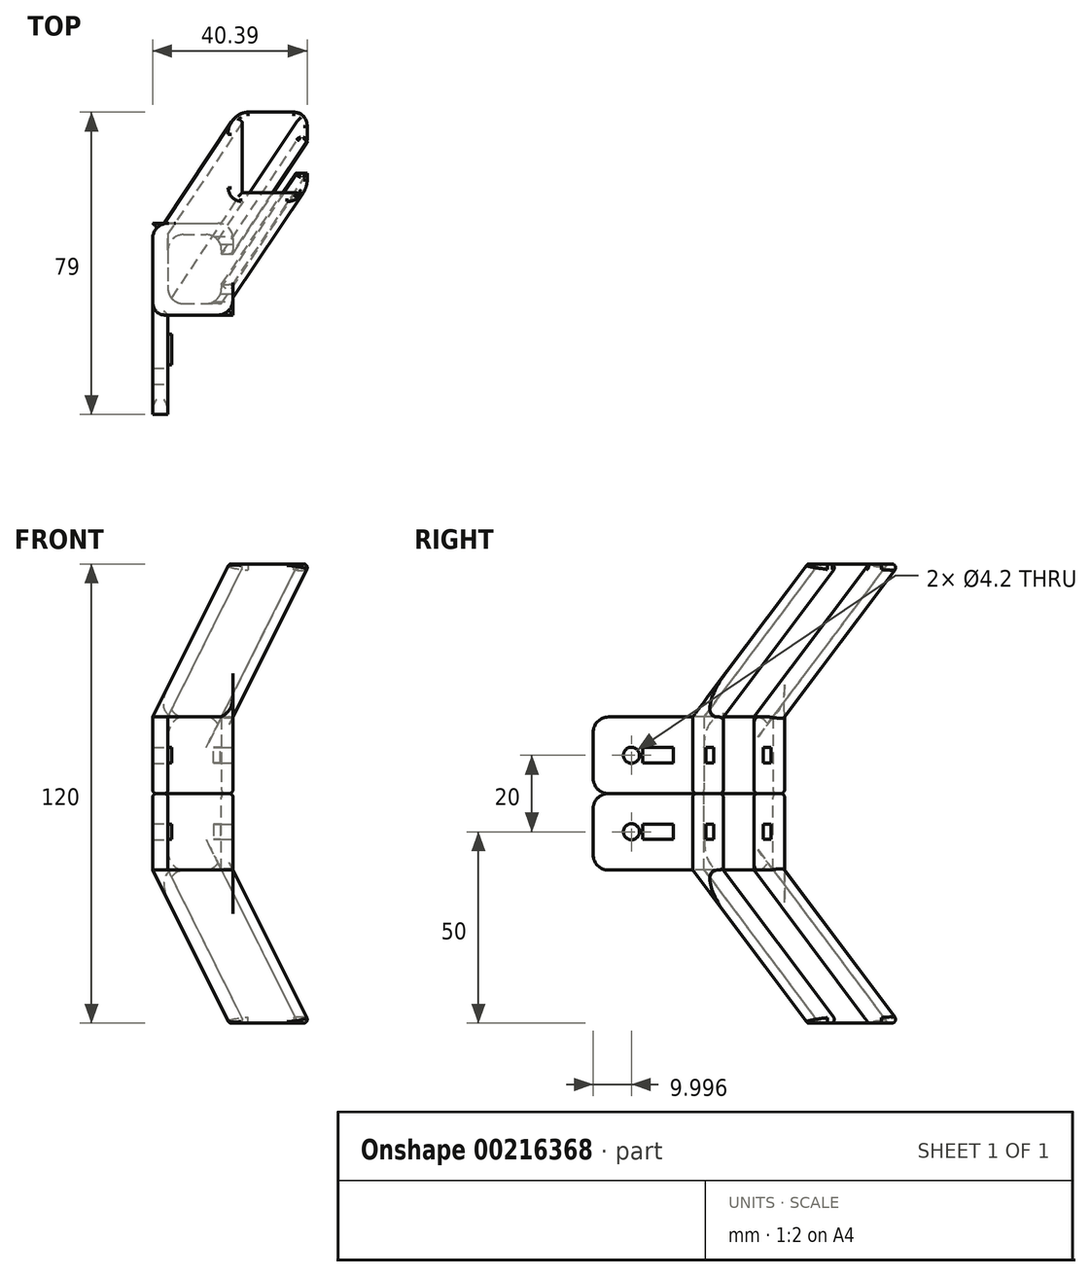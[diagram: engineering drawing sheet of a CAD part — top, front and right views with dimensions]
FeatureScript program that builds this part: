
annotation { "Feature Type Name" : "Feature", "Feature Type Description" : "" }
export const myFeature = defineFeature(function(context is Context, id is Id, definition is map)
    precondition{}
    {
        {
            var Q0;
            Q0=qCreatedBy(makeId("Top.planeOp"),FACE);
            var sketch = newSketch(context, id + "F0", { "sketchPlane" : qUnion([Q0])});
            skLineSegment(sketch, "E0.bottom", {"start": v(-48.62, 57.86) * mm, "end": v(-44.62, 57.86) * mm});
            skLineSegment(sketch, "E0.top", {"start": v(-48.62, 7.86) * mm, "end": v(-44.62, 7.86) * mm});
            skLineSegment(sketch, "E0.left", {"start": v(-48.62, 57.86) * mm, "end": v(-48.62, 7.86) * mm});
            skLineSegment(sketch, "E0.right", {"start": v(-44.62, 33.86) * mm, "end": v(-44.62, 7.86) * mm});
            skLineSegment(sketch, "E1.bottom", {"start": v(-44.62, 57.86) * mm, "end": v(-27.62, 57.86) * mm});
            skLineSegment(sketch, "E1.top", {"start": v(-44.62, 33.86) * mm, "end": v(-27.62, 33.86) * mm});
            skLineSegment(sketch, "E1.right", {"start": v(-27.62, 57.86) * mm, "end": v(-27.62, 49.86) * mm});
            skLineSegment(sketch, "E2.bottom", {"start": v(-44.62, 54.86) * mm, "end": v(-30.62, 54.86) * mm});
            skLineSegment(sketch, "E2.top", {"start": v(-44.62, 36.86) * mm, "end": v(-30.62, 36.86) * mm});
            skLineSegment(sketch, "E2.left", {"start": v(-44.62, 54.86) * mm, "end": v(-44.62, 36.86) * mm});
            skLineSegment(sketch, "E2.right", {"start": v(-30.62, 54.86) * mm, "end": v(-30.62, 49.86) * mm});
            skLineSegment(sketch, "E3", {"start": v(-30.62, 49.86) * mm, "end": v(-27.62, 49.86) * mm});
            skLineSegment(sketch, "E4", {"start": v(-30.62, 41.86) * mm, "end": v(-27.62, 41.86) * mm});
            skLineSegment(sketch, "E5.trimOffspring", {"start": v(-27.62, 41.86) * mm, "end": v(-27.62, 33.86) * mm});
            skLineSegment(sketch, "E6.trimOffspring", {"start": v(-30.62, 41.86) * mm, "end": v(-30.62, 36.86) * mm});
            skSolve(sketch);
        }
        {
            var Q0;
            Q0 = qSketchRegion(id + "F0", true);
            extrude(context, id + "F1", {"entities" : qUnion([Q0]), "depth" : 20 * mm, "offsetDistance" : 25 * mm});
        }
        {
            var Q0;
            Q0=makeQuery(id+"F1.opExtrude","SWEPT_FACE",FACE,{"disambiguationData":[OSD([sQuery(id+"F0.wireOp",EDGE,"E0.right")])]});
            var sketch = newSketch(context, id + "F2", { "sketchPlane" : qUnion([Q0])});
            skCircle(sketch, "E7", {"center": v(17.86, 10) * mm, "radius": 2.1 * mm});
            skPoint(sketch, "E7.centerSnap0", {"position": v(7.86, 10) * mm});
            skLineSegment(sketch, "E8.bottom", {"start": v(28.86, 12) * mm, "end": v(20.86, 12) * mm});
            skLineSegment(sketch, "E8.top", {"start": v(28.86, 8) * mm, "end": v(20.86, 8) * mm});
            skLineSegment(sketch, "E8.left", {"start": v(28.86, 12) * mm, "end": v(28.86, 8) * mm});
            skLineSegment(sketch, "E8.right", {"start": v(20.86, 12) * mm, "end": v(20.86, 8) * mm});
            skSolve(sketch);
        }
        {
            var Q0;
            Q0=makeQuery(id+"F2.imprint","IMPRINT",FACE,{"disambiguationData":[TD([[makeQuery(id+"F2.imprint","IMPRINT",EDGE,{"derivedFrom":sQuery(id+"F2.wireOp",EDGE,"E7")}),1.0]])]});
            extrude(context, id + "F3", {"entities" : qUnion([Q0]), "operationType" : NewBodyOperationType.REMOVE, "oppositeDirection" : true, "depth" : 25 * mm, "offsetDistance" : 25 * mm});
        }
        {
            var Q0;
            Q0=makeQuery(id+"F1.opExtrude","SWEPT_FACE",FACE,{"disambiguationData":[OSD([sQuery(id+"F0.wireOp",EDGE,"E1.right")])]});
            var sketch = newSketch(context, id + "F4", { "sketchPlane" : qUnion([Q0])});
            skLineSegment(sketch, "E9.bottom", {"start": v(54.36, 12) * mm, "end": v(52.36, 12) * mm});
            skLineSegment(sketch, "E9.top", {"start": v(54.36, 8) * mm, "end": v(52.36, 8) * mm});
            skLineSegment(sketch, "E9.left", {"start": v(54.36, 12) * mm, "end": v(54.36, 8) * mm});
            skLineSegment(sketch, "E9.right", {"start": v(52.36, 12) * mm, "end": v(52.36, 8) * mm});
            skSolve(sketch);
        }
        {
            var Q0;
            Q0=makeQuery(id+"F1.opExtrude","SWEPT_FACE",FACE,{"disambiguationData":[OSD([sQuery(id+"F0.wireOp",EDGE,"E5.trimOffspring")])]});
            var sketch = newSketch(context, id + "F5", { "sketchPlane" : qUnion([Q0])});
            skLineSegment(sketch, "E10.bottom", {"start": v(39.36, 12) * mm, "end": v(37.36, 12) * mm});
            skLineSegment(sketch, "E10.top", {"start": v(39.36, 8) * mm, "end": v(37.36, 8) * mm});
            skLineSegment(sketch, "E10.left", {"start": v(39.36, 12) * mm, "end": v(39.36, 8) * mm});
            skLineSegment(sketch, "E10.right", {"start": v(37.36, 12) * mm, "end": v(37.36, 8) * mm});
            skSolve(sketch);
        }
        {
            var Q0;
            Q0=makeQuery(id+"F4.imprint","IMPRINT",FACE,{"disambiguationData":[TD([[makeQuery(id+"F4.imprint","IMPRINT",EDGE,{"derivedFrom":sQuery(id+"F4.wireOp",EDGE,"E9.bottom")}),1.0]])]});
            var Q1;
            Q1=makeQuery(id+"F5.imprint","IMPRINT",FACE,{"disambiguationData":[TD([[makeQuery(id+"F5.imprint","IMPRINT",EDGE,{"derivedFrom":sQuery(id+"F5.wireOp",EDGE,"E10.bottom")}),1.0]])]});
            extrude(context, id + "F6", {"entities" : qUnion([Q0, Q1]), "operationType" : NewBodyOperationType.REMOVE, "oppositeDirection" : true, "depth" : 4 * mm, "offsetDistance" : 25 * mm});
        }
        {
            var Q0;
            Q0=makeQuery(id+"F1.opExtrude","CAP_FACE",FACE,{"disambiguationData":[OSD([sQuery(id+"F0.wireOp",EDGE,"E0.bottom"),sQuery(id+"F0.wireOp",EDGE,"E0.top"),sQuery(id+"F0.wireOp",EDGE,"E0.left"),sQuery(id+"F0.wireOp",EDGE,"E0.right"),sQuery(id+"F0.wireOp",EDGE,"E1.bottom"),sQuery(id+"F0.wireOp",EDGE,"E1.top"),sQuery(id+"F0.wireOp",EDGE,"E1.right"),sQuery(id+"F0.wireOp",EDGE,"E2.bottom"),sQuery(id+"F0.wireOp",EDGE,"E2.top"),sQuery(id+"F0.wireOp",EDGE,"E2.left"),sQuery(id+"F0.wireOp",EDGE,"E2.right"),sQuery(id+"F0.wireOp",EDGE,"E3"),sQuery(id+"F0.wireOp",EDGE,"E4"),sQuery(id+"F0.wireOp",EDGE,"E5.trimOffspring"),sQuery(id+"F0.wireOp",EDGE,"E6.trimOffspring")])],"isStart":false});
            var sketch = newSketch(context, id + "F7", { "sketchPlane" : qUnion([Q0])});
            skLineSegment(sketch, "E11", {"start": v(-44.62, 33.86) * mm, "end": v(-48.62, 33.86) * mm});
            skSolve(sketch);
        }
        {
            var Q0;
            Q0=makeQuery(id+"F1.opExtrude","CAP_FACE",FACE,{"disambiguationData":[OSD([sQuery(id+"F0.wireOp",EDGE,"E0.bottom"),sQuery(id+"F0.wireOp",EDGE,"E0.top"),sQuery(id+"F0.wireOp",EDGE,"E0.left"),sQuery(id+"F0.wireOp",EDGE,"E0.right"),sQuery(id+"F0.wireOp",EDGE,"E1.bottom"),sQuery(id+"F0.wireOp",EDGE,"E1.top"),sQuery(id+"F0.wireOp",EDGE,"E1.right"),sQuery(id+"F0.wireOp",EDGE,"E2.bottom"),sQuery(id+"F0.wireOp",EDGE,"E2.top"),sQuery(id+"F0.wireOp",EDGE,"E2.left"),sQuery(id+"F0.wireOp",EDGE,"E2.right"),sQuery(id+"F0.wireOp",EDGE,"E3"),sQuery(id+"F0.wireOp",EDGE,"E4"),sQuery(id+"F0.wireOp",EDGE,"E5.trimOffspring"),sQuery(id+"F0.wireOp",EDGE,"E6.trimOffspring")])],"isStart":false});
            cPlane(context, id + "F8", {"entities" : qUnion([Q0]), "cplaneType" : CPlaneType.OFFSET, "offset" : 40 * mm, "width" : 150 * mm, "height" : 150 * mm});
        }
        {
            var Q0;
            Q0=qCreatedBy(id+"F8.planeOp",FACE);
            var sketch = newSketch(context, id + "F9", { "sketchPlane" : qUnion([Q0])});
            skLineSegment(sketch, "E12.bottom", {"start": v(-28.62, 87.86) * mm, "end": v(-7.62, 87.86) * mm});
            skLineSegment(sketch, "E12.top", {"start": v(-28.62, 63.86) * mm, "end": v(-7.62, 63.86) * mm});
            skLineSegment(sketch, "E12.left", {"start": v(-28.62, 87.86) * mm, "end": v(-28.62, 63.86) * mm});
            skLineSegment(sketch, "E12.right", {"start": v(-7.62, 87.86) * mm, "end": v(-7.62, 79.86) * mm});
            skLineSegment(sketch, "E13.bottom", {"start": v(-24.62, 84.86) * mm, "end": v(-10.62, 84.86) * mm});
            skLineSegment(sketch, "E13.top", {"start": v(-24.62, 66.86) * mm, "end": v(-10.62, 66.86) * mm});
            skLineSegment(sketch, "E13.left", {"start": v(-24.62, 84.86) * mm, "end": v(-24.62, 66.86) * mm});
            skLineSegment(sketch, "E13.right", {"start": v(-10.62, 84.86) * mm, "end": v(-10.62, 79.86) * mm});
            skLineSegment(sketch, "E14", {"start": v(-7.62, 71.86) * mm, "end": v(-10.62, 71.86) * mm});
            skLineSegment(sketch, "E15", {"start": v(-7.62, 79.86) * mm, "end": v(-10.62, 79.86) * mm});
            skLineSegment(sketch, "E16.trimOffspring", {"start": v(-10.62, 71.86) * mm, "end": v(-10.62, 66.86) * mm});
            skLineSegment(sketch, "E17.trimOffspring", {"start": v(-7.62, 71.86) * mm, "end": v(-7.62, 63.86) * mm});
            skPoint(sketch, "E18", {"position": v(-24.62, 63.86) * mm});
            skSolve(sketch);
        }
        {
            var Q1;
            {var subQ0=sQuery(id+"F7.wireOp",EDGE,"E11");Q1=makeQuery(id+"F7.imprint","IMPRINT",FACE,{"disambiguationData":[TD([[makeQuery(id+"F7.imprint","IMPRINT",EDGE,{"derivedFrom":subQ0}),-1.0]])]});}
            var Q2;
            Q2=makeQuery(id+"F9.imprint","IMPRINT",FACE,{"disambiguationData":[TD([[makeQuery(id+"F9.imprint","IMPRINT",EDGE,{"derivedFrom":sQuery(id+"F9.wireOp",EDGE,"E12.bottom")}),-1.0]])]});
            var Q3;
            Q3=sQuery(id+"F7.wireOp",VERTEX,"E11.start");
            var Q4;
            Q4=sQuery(id+"F9.wireOp",VERTEX,"E18");
            loft(context, id + "F10", {"operationType" : NewBodyOperationType.ADD, "sheetProfilesArray" : [{ "sheetProfileEntities" : qUnion([Q1]) }, { "sheetProfileEntities" : qUnion([Q2]) }], "matchConnections" : true, "connections" : [{ "connectionEntities" : qUnion([Q3, Q4]), "connectionEdgeQueries" : qUnion([]), "connectionEdgeParameters" : [] }]});
        }
        {
            var Q0;
            Q0=makeQuery(id+"F1.opExtrude","CAP_EDGE",EDGE,{"disambiguationData":[OSD([sQuery(id+"F0.wireOp",EDGE,"E0.top")])],"isStart":false});
            var Q1;
            Q1=makeQuery(id+"F1.opExtrude","CAP_EDGE",EDGE,{"disambiguationData":[OSD([sQuery(id+"F0.wireOp",EDGE,"E0.top")])],"isStart":true});
            var Q2;
            Q2=makeQuery(id+"F1.opExtrude","SWEPT_EDGE",EDGE,{"disambiguationData":[OSD([sQuery(id+"F0.wireOp",EDGE,"E2.top"),sQuery(id+"F0.wireOp",EDGE,"E6.trimOffspring")])]});
            var Q3;
            Q3=makeQuery(id+"F1.opExtrude","SWEPT_EDGE",EDGE,{"disambiguationData":[OSD([sQuery(id+"F0.wireOp",EDGE,"E2.bottom"),sQuery(id+"F0.wireOp",EDGE,"E2.right")])]});
            var Q4;
            Q4=makeQuery(id+"F1.opExtrude","SWEPT_EDGE",EDGE,{"disambiguationData":[OSD([sQuery(id+"F0.wireOp",EDGE,"E2.bottom"),sQuery(id+"F0.wireOp",EDGE,"E2.left")])]});
            var Q5;
            Q5=makeQuery(id+"F1.opExtrude","SWEPT_EDGE",EDGE,{"disambiguationData":[OSD([sQuery(id+"F0.wireOp",EDGE,"E2.top"),sQuery(id+"F0.wireOp",EDGE,"E2.left")])]});
            var Q6;
            Q6=makeQuery(id+"F10.opLoft","SWEPT_EDGE",EDGE,{"disambiguationData":[OSD([sQuery(id+"F0.wireOp",EDGE,"E0.bottom"),sQuery(id+"F0.wireOp",EDGE,"E1.bottom"),sQuery(id+"F0.wireOp",EDGE,"E1.right"),sQuery(id+"F9.wireOp",EDGE,"E12.bottom"),sQuery(id+"F9.wireOp",EDGE,"E12.right")])]});
            var Q7;
            Q7=makeQuery(id+"F10.opLoft","SWEPT_EDGE",EDGE,{"disambiguationData":[OSD([sQuery(id+"F0.wireOp",EDGE,"E0.left"),sQuery(id+"F7.wireOp",EDGE,"E11"),sQuery(id+"F9.wireOp",EDGE,"E12.top"),sQuery(id+"F9.wireOp",EDGE,"E12.left")])]});
            var Q8;
            Q8=makeQuery(id+"F1.opExtrude","SWEPT_EDGE",EDGE,{"disambiguationData":[OSD([sQuery(id+"F0.wireOp",EDGE,"E1.bottom"),sQuery(id+"F0.wireOp",EDGE,"E1.right")])]});
            var Q9;
            Q9=makeQuery(id+"F10.opLoft","SWEPT_EDGE",EDGE,{"disambiguationData":[OSD([sQuery(id+"F0.wireOp",EDGE,"E1.top"),sQuery(id+"F0.wireOp",EDGE,"E5.trimOffspring"),sQuery(id+"F9.wireOp",EDGE,"E12.top"),sQuery(id+"F9.wireOp",EDGE,"E17.trimOffspring")])]});
            var Q10;
            Q10=makeQuery(id+"F10.opLoft","SWEPT_EDGE",EDGE,{"disambiguationData":[OSD([sQuery(id+"F0.wireOp",EDGE,"E0.bottom"),sQuery(id+"F0.wireOp",EDGE,"E0.left"),sQuery(id+"F0.wireOp",EDGE,"E1.bottom"),sQuery(id+"F9.wireOp",EDGE,"E12.bottom"),sQuery(id+"F9.wireOp",EDGE,"E12.left")])]});
            fillet(context, id + "F11", {"entities" : qUnion([Q0, Q1, Q2, Q3, Q4, Q5, Q6, Q7, Q8, Q9, Q10]), "radius" : 4 * mm, "allowEdgeOverflow" : false});
        }
        {
            var Q0;
            Q0=makeQuery(id+"F10.opLoft","CAP_FACE",FACE,{"disambiguationData":[OSD([makeQuery(id+"F9.imprint","IMPRINT",FACE,{"disambiguationData":[TD([[makeQuery(id+"F9.imprint","IMPRINT",EDGE,{"derivedFrom":sQuery(id+"F9.wireOp",EDGE,"E12.bottom")}),-1.0]])]})])],"isStart":true});
            var Q1;
            Q1=makeQuery(id+"F1.opExtrude","CAP_FACE",FACE,{"disambiguationData":[OSD([sQuery(id+"F0.wireOp",EDGE,"E0.bottom"),sQuery(id+"F0.wireOp",EDGE,"E0.top"),sQuery(id+"F0.wireOp",EDGE,"E0.left"),sQuery(id+"F0.wireOp",EDGE,"E0.right"),sQuery(id+"F0.wireOp",EDGE,"E1.bottom"),sQuery(id+"F0.wireOp",EDGE,"E1.top"),sQuery(id+"F0.wireOp",EDGE,"E1.right"),sQuery(id+"F0.wireOp",EDGE,"E2.bottom"),sQuery(id+"F0.wireOp",EDGE,"E2.top"),sQuery(id+"F0.wireOp",EDGE,"E2.left"),sQuery(id+"F0.wireOp",EDGE,"E2.right"),sQuery(id+"F0.wireOp",EDGE,"E3"),sQuery(id+"F0.wireOp",EDGE,"E4"),sQuery(id+"F0.wireOp",EDGE,"E5.trimOffspring"),sQuery(id+"F0.wireOp",EDGE,"E6.trimOffspring")])],"isStart":true});
            var Q2;
            Q2=makeQuery(id+"F1.opExtrude","SWEPT_EDGE",EDGE,{"disambiguationData":[OSD([sQuery(id+"F0.wireOp",EDGE,"E4"),sQuery(id+"F0.wireOp",EDGE,"E5.trimOffspring")])]});
            var Q3;
            Q3=makeQuery(id+"F1.opExtrude","SWEPT_EDGE",EDGE,{"disambiguationData":[OSD([sQuery(id+"F0.wireOp",EDGE,"E1.right"),sQuery(id+"F0.wireOp",EDGE,"E3")])]});
            fillet(context, id + "F12", {"entities" : qUnion([Q0, Q1, Q2, Q3]), "radius" : 1 * mm, "allowEdgeOverflow" : false});
        }
        {
            var Q0;
            Q0=makeQuery(id+"F2.imprint","IMPRINT",FACE,{"disambiguationData":[TD([[makeQuery(id+"F2.imprint","IMPRINT",EDGE,{"derivedFrom":sQuery(id+"F2.wireOp",EDGE,"E8.bottom")}),1.0]])]});
            extrude(context, id + "F13", {"entities" : qUnion([Q0]), "operationType" : NewBodyOperationType.ADD, "depth" : 1 * mm, "offsetDistance" : 25 * mm});
        }
        {
            var Q0;
            Q0=makeQuery(id+"F1.opExtrude","SWEPT_BODY",BODY,{"disambiguationData":[OSD([sQuery(id+"F0.wireOp",EDGE,"E0.bottom"),sQuery(id+"F0.wireOp",EDGE,"E0.top"),sQuery(id+"F0.wireOp",EDGE,"E0.left"),sQuery(id+"F0.wireOp",EDGE,"E0.right"),sQuery(id+"F0.wireOp",EDGE,"E1.bottom"),sQuery(id+"F0.wireOp",EDGE,"E1.top"),sQuery(id+"F0.wireOp",EDGE,"E1.right"),sQuery(id+"F0.wireOp",EDGE,"E2.bottom"),sQuery(id+"F0.wireOp",EDGE,"E2.top"),sQuery(id+"F0.wireOp",EDGE,"E2.left"),sQuery(id+"F0.wireOp",EDGE,"E2.right"),sQuery(id+"F0.wireOp",EDGE,"E3"),sQuery(id+"F0.wireOp",EDGE,"E4"),sQuery(id+"F0.wireOp",EDGE,"E5.trimOffspring"),sQuery(id+"F0.wireOp",EDGE,"E6.trimOffspring")])]});
            var Q1;
            Q1=qCreatedBy(makeId("Top.planeOp"),FACE);
            mirror(context, id + "F14", {"entities" : qUnion([Q0]), "mirrorPlane" : qUnion([Q1])});
        }
        {
            var Q0;
            Q0=makeQuery(id+"F1.opExtrude","SWEPT_EDGE",EDGE,{"disambiguationData":[OSD([sQuery(id+"F0.wireOp",EDGE,"E0.bottom"),sQuery(id+"F0.wireOp",EDGE,"E0.left")])]});
            var Q1;
            Q1=makeQuery(id+"F1.opExtrude","SWEPT_EDGE",EDGE,{"disambiguationData":[OSD([sQuery(id+"F0.wireOp",EDGE,"E1.top"),sQuery(id+"F0.wireOp",EDGE,"E5.trimOffspring")])]});
            fillet(context, id + "F15", {"entities" : qUnion([Q0, Q1]), "radius" : 4 * mm, "tangentPropagation" : true, "allowEdgeOverflow" : false});
        }
        {
            var Q0;
            Q0=makeQuery(id+"F10.opLoft","SWEPT_EDGE",EDGE,{"disambiguationData":[OSD([sQuery(id+"F0.wireOp",EDGE,"E4"),sQuery(id+"F0.wireOp",EDGE,"E5.trimOffspring"),sQuery(id+"F9.wireOp",EDGE,"E14"),sQuery(id+"F9.wireOp",EDGE,"E17.trimOffspring")])]});
            var Q1;
            Q1=makeQuery(id+"F10.opLoft","SWEPT_EDGE",EDGE,{"disambiguationData":[OSD([sQuery(id+"F0.wireOp",EDGE,"E1.right"),sQuery(id+"F0.wireOp",EDGE,"E3"),sQuery(id+"F9.wireOp",EDGE,"E12.right"),sQuery(id+"F9.wireOp",EDGE,"E15")])]});
            var Q2;
            Q2=makeQuery(id+"F10.opLoft","SWEPT_EDGE",EDGE,{"disambiguationData":[OSD([sQuery(id+"F0.wireOp",EDGE,"E2.right"),sQuery(id+"F0.wireOp",EDGE,"E3"),sQuery(id+"F9.wireOp",EDGE,"E13.right"),sQuery(id+"F9.wireOp",EDGE,"E15")])]});
            var Q3;
            Q3=makeQuery(id+"F10.opLoft","SWEPT_EDGE",EDGE,{"disambiguationData":[OSD([sQuery(id+"F0.wireOp",EDGE,"E4"),sQuery(id+"F0.wireOp",EDGE,"E6.trimOffspring"),sQuery(id+"F9.wireOp",EDGE,"E14"),sQuery(id+"F9.wireOp",EDGE,"E16.trimOffspring")])]});
            fillet(context, id + "F16", {"entities" : qUnion([Q0, Q1, Q2, Q3]), "radius" : 0.5 * mm, "tangentPropagation" : true, "allowEdgeOverflow" : false});
        }
    });
